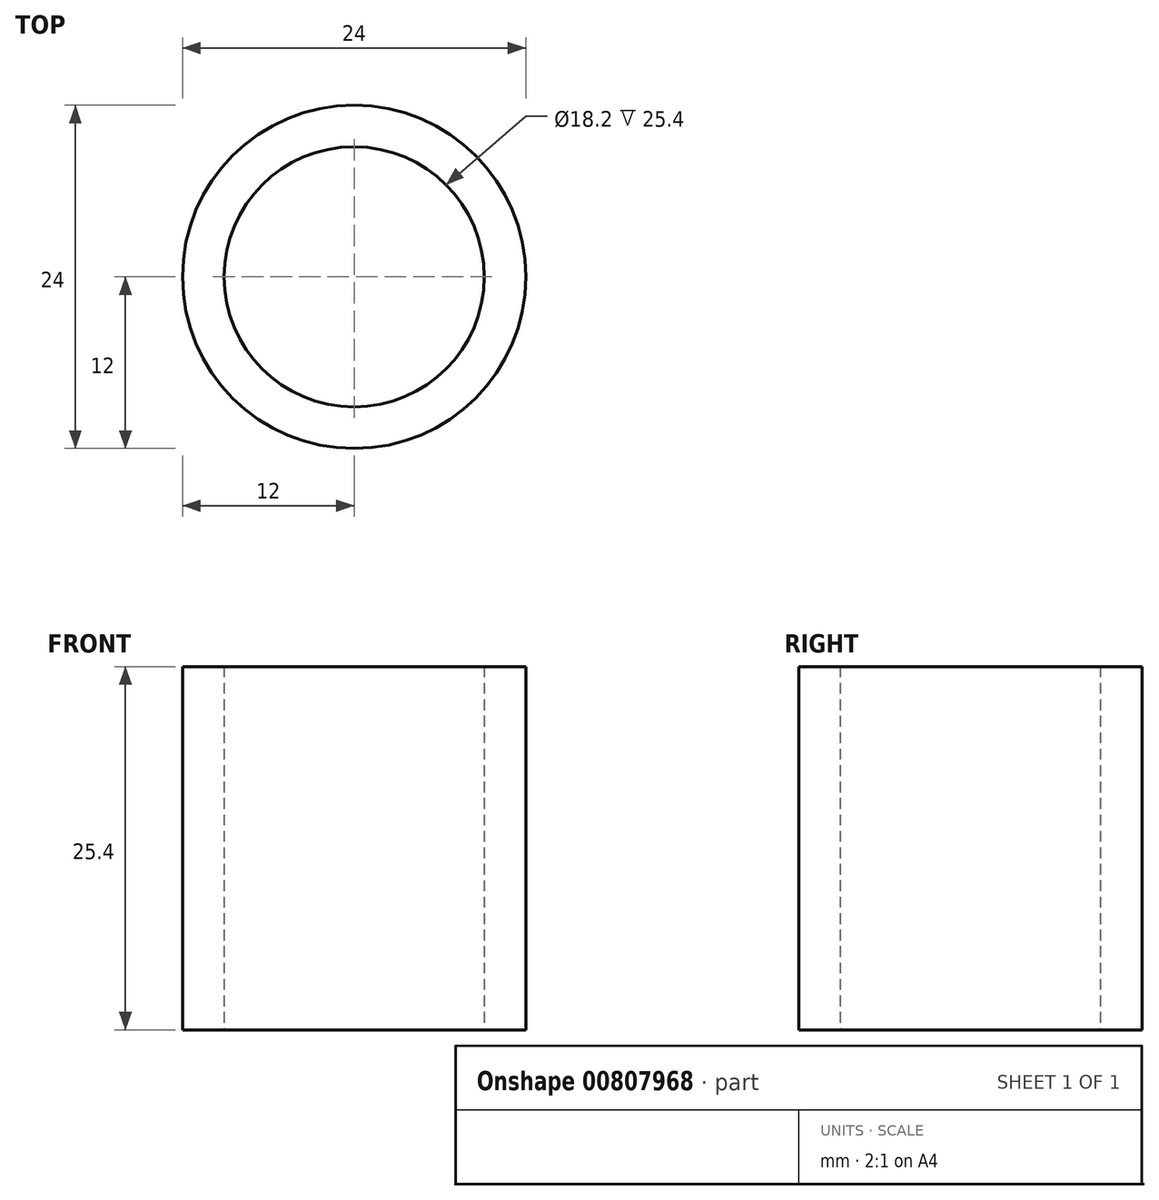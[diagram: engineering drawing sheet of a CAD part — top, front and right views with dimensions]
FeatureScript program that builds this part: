
annotation { "Feature Type Name" : "Feature", "Feature Type Description" : "" }
export const myFeature = defineFeature(function(context is Context, id is Id, definition is map)
    precondition{}
    {
        {
            var Q0;
            Q0=qCreatedBy(makeId("Top.planeOp"),FACE);
            var sketch = newSketch(context, id + "F0", { "sketchPlane" : qUnion([Q0])});
            skCircle(sketch, "E0", {"center": v(0, 0) * mm, "radius": 12 * mm});
            skCircle(sketch, "E1", {"center": v(0, 0) * mm, "radius": 9.1 * mm});
            skSolve(sketch);
        }
        {
            var Q0;
            Q0 = qSketchRegion(id + "F0", true);
            extrude(context, id + "F1", {"entities" : qUnion([Q0]), "depth" : 25.4 * mm, "offsetDistance" : 25.4 * mm});
        }
    });
